# Revit family: Hand_Dryer-Excel_Dryer-XLERATOR_Unit
name_source: partatom
category: Specialty Equipment
revit_build: Autodesk Revit 2017 (Build: 20190508_0315(x64)
units: mm (PartAtom-declared; Revit-internal decimal feet)

## family parameters
Cut with Voids When Loaded = No
Host = Face
OmniClass Number = 23.40.20.21.14
OmniClass Title = Hand and Hair Dryers
Part Type = Normal
Room Calculation Point = No
Round Connector Dimension = Use Diameter
Shared = No

## types (1)
- Hand_Dryer-Excel_Dryer-XLERATOR_Unit
    ADA Compliance = http://www.exceldryer.com
    Air Temperature (Farenheit) = 135 °F
    Amperage = 0 A
    Apparent Load = 1500 VA
    Assembly Code = C1030200
    Cost Information = http://www.exceldryer.com
    Cost Savings Analysis = http://www.exceldryer.com
    Cover Finish = Metal - Excel Dryer - Chrome - Polished
    Cover Material = Thermoset BMC
    Default Elevation = 3' - 5"
    Depth = 0' - 6 7/8"
    Description = XLERATOR Hand Dryer
    Dry Time = 10-15 Seconds
    Expected Lifespan = 15+ Years
    Frequency = 60 Hz
    Green Building LEED = http://www.exceldryer.com
    Heating Element = 900 Watts
    Height = 1' - 0 7/8"
    Impact Resistant Note = UL 499
    Installation Phase = Single
    Keynote = 10 28 13
    Maintenance Schedule = Once to Twice per Year
    Manufacturer = Excel Dryer
    Manufacturer Fax Number = 1-413-525-2853
    Model = Wall Guard White
    Motor Note = 12.5 A@110/120V Single phase (4.5A eco); 7.0 A @208V Single phase (2.1A eco); 6.5 A @220/240V Single phase(2.2A eco); 5.5 A @277V Single phase (no eco available).
    Mounting Note = For correct placement, match Elevation to Mounting Height.
    Noise Reduction Nozzle Product Documentation Link = http://www.exceldryer.com
    Number of Poles = 1
    Output at Outlet (LFM) = 16000
    Phase = 1
    Power Factor = 1
    Product Documentation Link = https://www.exceldryer.com
    Product Name = XLERATOR Hand Dryer
    Product Page URL = https://www.exceldryer.com
    Product Weight = 17lbs
    Run-Time Cycle = Automatic
    Time Cycle = Automatic
    URL = http://www.exceldryer.com
    Version = 2017 - v1.0b
    Void = 0' - 0 1/16"
    Void Depth = 7' - 5 15/16"
    Voltage = 120 V
    Warranty Duration = 5 Years
    Watts = 15000 W
    Width = 0' - 11 15/16"

## geometry (parser evidence)
native form markers: Sweep x3
no freeform markers — native parametric forms only
